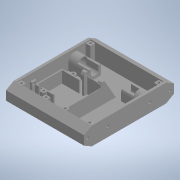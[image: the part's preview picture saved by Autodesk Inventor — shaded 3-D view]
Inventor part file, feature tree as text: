
AUTODESK INVENTOR PART (.ipt)
format: ipt  version: 2020 (Build 240168000, 168)  size: 610,304 bytes
history: native  units: in
note: dims shown in document units (in); Inventor stores cm internally (conversion verified against a paired STEP export)
features: extrude x18, sketch x17, projected_geometry x14, mirror x6, plane x1
ambient origin geometry x8: Origin, YZ Plane, XZ Plane, XY Plane, X Axis, Y Axis, Z Axis, Center Point
bodies: Solid1 (feature_tree)
feature tree (56):
  extrude  "Extrusion1"  Depth=5.9055in
  extrude  "Extrusion2"  TaperAngle=0.0deg  [1 undecoded]
  extrude  "Extrusion3"  Depth=1.063in
  extrude  "Extrusion4"  Depth=0.315in
  extrude  "Extrusion5"  TaperAngle=0.0deg  [1 undecoded]
  extrude  "Extrusion6"  Depth=0.5906in
  mirror  "Mirror1"
  extrude  "Extrusion7"  Depth=0.0787in
  mirror  "Mirror2"
  extrude  "Extrusion8"  Depth=0.6102in
  mirror  "Mirror3"
  plane  "Work Plane1"
  extrude  "Extrusion9"  Depth=0.7874in TaperAngle=0.0deg
  mirror  "Mirror4"
  extrude  "Extrusion10"  Depth=0.1654in TaperAngle=0.0deg
  extrude  "Extrusion11"  Depth=0.1575in
  extrude  "Extrusion12"  TaperAngle=0.0deg  [1 undecoded]
  extrude  "Extrusion13"  Depth=0.2756in
  extrude  "Extrusion14"  Depth=0.4331in
  extrude  "Extrusion17"  Depth=2.7559in
  extrude  "Extrusion18"  Depth=0.061in
  mirror  "Mirror6"
  extrude  "Extrusion19"  TaperAngle=0.0deg  [1 undecoded]
  mirror  "Mirror7"
  extrude  "Extrusion20"  TaperAngle=60.0deg  [1 undecoded]
  sketch  "Sketch1"  dims[d0=1.1811in d1=5.9055in]
  sketch  "Sketch2"  dims[d2=5.1181in d3=0.0in]
  projected_geometry  "Projected Loop1"
  sketch  "Sketch3"  dims[d4=0.1575in d5=1.063in]
  projected_geometry  "Projected Loop2"
  projected_geometry  "Projected Loop3"
  sketch  "Sketch4"  dims[d6=0.0in d8=0.315in]
  projected_geometry  "Projected Loop4"
  sketch  "Sketch6"  dims[d10=0.993in d11=0.0in]
  sketch  "Sketch7"  dims[d12=0.6496in d13=0.5906in]
  sketch  "Sketch9"  dims[d14=1.5748in d15=0.0787in]
  sketch  "Sketch10"  dims[d16=0.5512in d17=0.0in d18=0.6102in]
  sketch  "Sketch12"  dims[d19=0.4803in d20=0.7874in d21=0.0in]
  projected_geometry  "Projected Loop6"
  projected_geometry  "Projected Loop7"
  projected_geometry  "Projected Loop8"
  sketch  "Sketch13"  dims[d22=0.1654in d23=6.063in d24=0.0in]
  sketch  "Sketch14"  dims[d25=0.5114in d26=0.1575in]
  sketch  "Sketch15"  dims[d27=1.5748in d28=0.0in d29=0.0in]
  projected_geometry  "Projected Loop15"
  sketch  "Sketch16"  dims[d30=0.1575in d31=0.2756in]
  projected_geometry  "Projected Loop19"
  projected_geometry  "Projected Loop20"
  projected_geometry  "Projected Loop21"
  projected_geometry  "Projected Loop22"
  projected_geometry  "Projected Loop23"
  projected_geometry  "Projected Loop24"
  sketch  "Sketch20"  dims[d32=0.0in d33=0.4331in]
  sketch  "Sketch21"  dims[d34=0.122in d38=2.7559in]
  sketch  "Sketch22"  dims[d40=0.061in d41=0.0909in]
  sketch  "Sketch23"  dims[d42=0.2362in d43=0.0in d44=60.0deg d45=0.0787in d46=0.315in d48=0.993in d49=0.0in d53=0.2756in d54=0.0in d55=0.4724in d56=1.2008in d57=1.6142in d58=1.5945in d59=0.0787in d60=0.0787in d62=0.315in d63=0.7677in d64=0.0in d66=0.1476in d67=0.2756in d68=0.0in d69=0.7874in d70=0.2953in d71=0.1181in d72=0.0in d89=0.0157in d90=0.0157in d91=0.1476in d92=0.1476in d96=0.315in d97=0.1575in d98=0.1181in d99=0.0in d102=0.1772in d104=0.3346in d105=135.0deg d106=0.2362in d107=0.0in d108=0.0394in d109=0.0in d110=0.0315in d111=0.0394in d112=0.0in d113=0.0315in]
note: 5 required parameter values undecoded (feature->parameter linkage not recoverable at this tier; creation-order binding heuristic only, values carry confidence <= 0.55)
